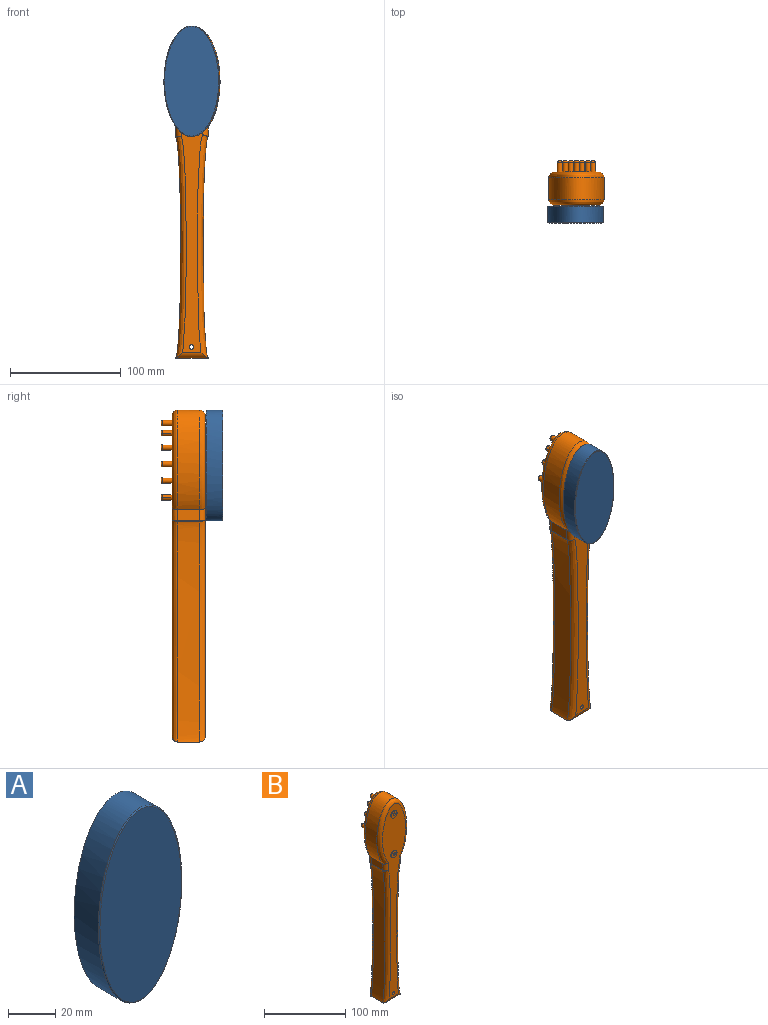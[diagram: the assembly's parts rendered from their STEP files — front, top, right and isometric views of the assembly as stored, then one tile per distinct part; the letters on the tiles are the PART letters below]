
ASSEMBLY  parts=2 mates=1
PART A: 12 faces, bbox 50x16x100 mm
  f0: extruded ~100x50mm, area 3512.2mm2, adj f2,f3
  f1: plane 99.01x49.01mm, normal (0,-1,0), area 3805.3mm2, adj f3
  f2: plane 100x50mm, normal (0,1,0), area 3769.9mm2, adj f0,f4,f6
  f3: bspline ~100.01x50.01mm, area 189.4mm2, adj f0,f1
  f4: cylinder r=5mm len=10mm, axis (0,1,0), area 31.4mm2, adj f2,f5
  f5: plane 10x10mm, normal (0,1,0), area 66mm2, adj f4,f10
  f6: cylinder r=5mm len=10mm, axis (0,1,0), area 31.4mm2, adj f2,f7
  f7: plane 10x10mm, normal (0,1,0), area 66mm2, adj f6,f8
  f8: cylinder r=2mm len=4mm, axis (0,-1,0), area 25.1mm2, adj f7,f9
  f9: plane 4x4mm, normal (0,1,0), area 12.6mm2, adj f8
  f10: cylinder r=2mm len=4mm, axis (0,-1,0), area 25.1mm2, adj f5,f11
  f11: plane 4x4mm, normal (0,1,0), area 12.6mm2, adj f10
PART B: 85 faces, bbox 50x41x305 mm
  f0: plane 290.01x40.01mm, normal (0,1,0), area 4887.9mm2, adj f9,f11,f12,f13,f14,f15,f23,f24
  f1: extruded ~91.05x49.99mm, area 4118.8mm2, adj f2,f7,f11,f18
  f2: plane 20x10mm, normal (-1,0,0), area 200mm2, adj f1,f3,f9,f17
  f3: plane 20x0.53mm, normal (-1,0,0), area 10.6mm2, adj f2,f4,f10,f16
  f4: extruded ~199.47x20mm, area 4000.7mm2, adj f3,f5,f12,f19
  f5: plane 29.27x20mm, normal (0,0,-1), area 585.5mm2, adj f4,f6,f14,f21
  f6: extruded ~200x20mm, area 4019.4mm2, adj f5,f7,f15,f22
  f7: plane 20x8.95mm, normal (1,0,0), area 178.9mm2, adj f1,f6,f13,f20
  f8: plane 290.01x40.01mm, normal (0,-1,0), area 5025.7mm2, adj f17,f18,f19,f20,f21,f22,f76,f78
  f9: cylinder r=5mm len=11.58mm, axis (0,0,-1), area 83.9mm2, adj f0,f2,f10,f11,f12
  f10: cylinder r=5mm len=4.11mm, axis (0,0,-1), area 1.3mm2, adj f3,f9,f12
  f11: bspline ~93.17x50.01mm, area 1567.7mm2, adj f0,f1,f9,f13
  f12: bspline ~206.01x9.7mm, area 1557.8mm2, adj f0,f4,f9,f10,f14
  f13: cylinder r=5mm len=10.63mm, axis (0,0,1), area 70.3mm2, adj f0,f7,f11,f15
  f14: cylinder r=5mm len=29.27mm, axis (1,0,0), area 179.2mm2, adj f0,f5,f12,f15
  f15: bspline ~210.02x10.6mm, area 1577.2mm2, adj f0,f6,f13,f14
  f16: cylinder r=5mm len=4.11mm, axis (0,0,1), area 1.3mm2, adj f3,f17,f19
  f17: cylinder r=5mm len=11.58mm, axis (0,0,1), area 83.9mm2, adj f2,f8,f16,f18,f19
  f18: bspline ~94.38x50.01mm, area 1568.1mm2, adj f1,f8,f17,f20
  f19: bspline ~206.01x9.7mm, area 1557.8mm2, adj f4,f8,f16,f17,f21
  f20: cylinder r=5mm len=10.63mm, axis (0,0,-1), area 70.3mm2, adj f7,f8,f18,f22
  f21: cylinder r=5mm len=29.27mm, axis (-1,0,0), area 179.2mm2, adj f5,f8,f19,f22
  f22: bspline ~210.02x10.6mm, area 1577.2mm2, adj f6,f8,f20,f21
  f23: extruded ~9x5mm, area 70.7mm2, adj f0,f24,f75
  f24: cylinder r=2.5mm len=9mm, axis (0,-1,0), area 70.7mm2, adj f0,f23,f74
  f25: plane 3x3mm, normal (0,1,0), area 7.1mm2, adj f74,f75
  f26: extruded ~9x5mm, area 70.7mm2, adj f0,f27,f73
  f27: cylinder r=2.5mm len=9mm, axis (0,-1,0), area 70.7mm2, adj f0,f26,f72
  f28: plane 3x3mm, normal (0,1,0), area 7.1mm2, adj f72,f73
  f29: cylinder r=2.5mm len=9mm, axis (0,-1,0), area 141.4mm2, adj f0,f70
  f30: plane 3x3mm, normal (0,1,0), area 7.1mm2, adj f70
  f31: cylinder r=2.5mm len=9mm, axis (0,-1,0), area 141.4mm2, adj f0,f69
  f32: plane 3x3mm, normal (0,1,0), area 7.1mm2, adj f69
  f33: cylinder r=2.5mm len=9mm, axis (0,-1,0), area 141.4mm2, adj f0,f68
  f34: plane 3x3mm, normal (0,1,0), area 7.1mm2, adj f68
  f35: cylinder r=2.5mm len=9mm, axis (0,-1,0), area 141.4mm2, adj f0,f66
  f36: plane 3x3mm, normal (0,1,0), area 7.1mm2, adj f66
  f37: cylinder r=2.5mm len=9mm, axis (0,-1,0), area 141.4mm2, adj f0,f65
  f38: plane 3x3mm, normal (0,1,0), area 7.1mm2, adj f65
  f39: cylinder r=2.5mm len=9mm, axis (0,-1,0), area 141.4mm2, adj f0,f64
  f40: plane 3x3mm, normal (0,1,0), area 7.1mm2, adj f64
  f41: cylinder r=2.5mm len=9mm, axis (0,-1,0), area 141.4mm2, adj f0,f67
  f42: plane 3x3mm, normal (0,1,0), area 7.1mm2, adj f67
  f43: cylinder r=2.5mm len=9mm, axis (0,-1,0), area 141.4mm2, adj f0,f61
  f44: plane 3x3mm, normal (0,1,0), area 7.1mm2, adj f61
  f45: cylinder r=2.5mm len=9mm, axis (0,-1,0), area 141.4mm2, adj f0,f62
  f46: plane 3x3mm, normal (0,1,0), area 7.1mm2, adj f62
  f47: cylinder r=2.5mm len=9mm, axis (0,-1,0), area 141.4mm2, adj f0,f63
  f48: plane 3x3mm, normal (0,1,0), area 7.1mm2, adj f63
  f49: cylinder r=2.5mm len=9mm, axis (0,-1,0), area 70.7mm2, adj f0,f50,f57
  f50: extruded ~9x5mm, area 70.7mm2, adj f0,f49,f58
  f51: plane 3x3mm, normal (0,1,0), area 7.1mm2, adj f57,f58
  f52: cylinder r=2.5mm len=9mm, axis (0,-1,0), area 70.7mm2, adj f0,f53,f59
  f53: extruded ~9x5mm, area 70.7mm2, adj f0,f52,f60
  f54: plane 3x3mm, normal (0,1,0), area 7.1mm2, adj f59,f60
  f55: cylinder r=2.5mm len=9mm, axis (0,-1,0), area 141.4mm2, adj f0,f71
  f56: plane 3x3mm, normal (0,1,0), area 7.1mm2, adj f71
  f57: torus R=1.5mm, axis (0,1,0), area 10.5mm2, adj f49,f51,f58
  f58: bspline ~5x3.5mm, area 10.5mm2, adj f50,f51,f57
  f59: torus R=1.5mm, axis (0,1,0), area 10.5mm2, adj f52,f54,f60
  f60: bspline ~5x3.5mm, area 10.5mm2, adj f53,f54,f59
  f61: torus R=1.5mm, axis (0,1,0), area 21.1mm2, adj f43,f44
  f62: torus R=1.5mm, axis (0,1,0), area 21.1mm2, adj f45,f46
  f63: torus R=1.5mm, axis (0,1,0), area 21.1mm2, adj f47,f48
  f64: torus R=1.5mm, axis (0,1,0), area 21.1mm2, adj f39,f40
  f65: torus R=1.5mm, axis (0,1,0), area 21.1mm2, adj f37,f38
  f66: torus R=1.5mm, axis (0,1,0), area 21.1mm2, adj f35,f36
  f67: torus R=1.5mm, axis (0,1,0), area 21.1mm2, adj f41,f42
  f68: torus R=1.5mm, axis (0,1,0), area 21.1mm2, adj f33,f34
  f69: torus R=1.5mm, axis (0,1,0), area 21.1mm2, adj f31,f32
  f70: torus R=1.5mm, axis (0,1,0), area 21.1mm2, adj f29,f30
  f71: torus R=1.5mm, axis (0,1,0), area 21.1mm2, adj f55,f56
  f72: torus R=1.5mm, axis (0,1,0), area 10.5mm2, adj f27,f28,f73
  f73: bspline ~5x3.5mm, area 10.5mm2, adj f26,f28,f72
  f74: torus R=1.5mm, axis (0,1,0), area 10.5mm2, adj f24,f25,f75
  f75: bspline ~5x3.5mm, area 10.5mm2, adj f23,f25,f74
  f76: cylinder r=5mm len=10mm, axis (0,1,0), area 31.4mm2, adj f8,f77
  f77: plane 10x10mm, normal (0,-1,0), area 66mm2, adj f76,f82
  f78: cylinder r=5mm len=10mm, axis (0,1,0), area 31.4mm2, adj f8,f79
  f79: plane 10x10mm, normal (0,-1,0), area 66mm2, adj f78,f80
  f80: cylinder r=2mm len=4mm, axis (0,-1,0), area 25.1mm2, adj f79,f81
  f81: plane 4x4mm, normal (0,-1,0), area 12.6mm2, adj f80
  f82: cylinder r=2mm len=4mm, axis (0,-1,0), area 25.1mm2, adj f77,f83
  f83: plane 4x4mm, normal (0,-1,0), area 12.6mm2, adj f82
  f84: cylinder r=2mm len=30mm, axis (0,1,0), area 377mm2, adj f0,f8
PLACE A t=(-208.89,-33.67,259.65)mm
PLACE B t=(-223.89,-2.67,9.65)mm
MATE fastened A.f6 <-> B.f76  axis (0,1,0) through (-208.89,-33.67,289.65)mm
